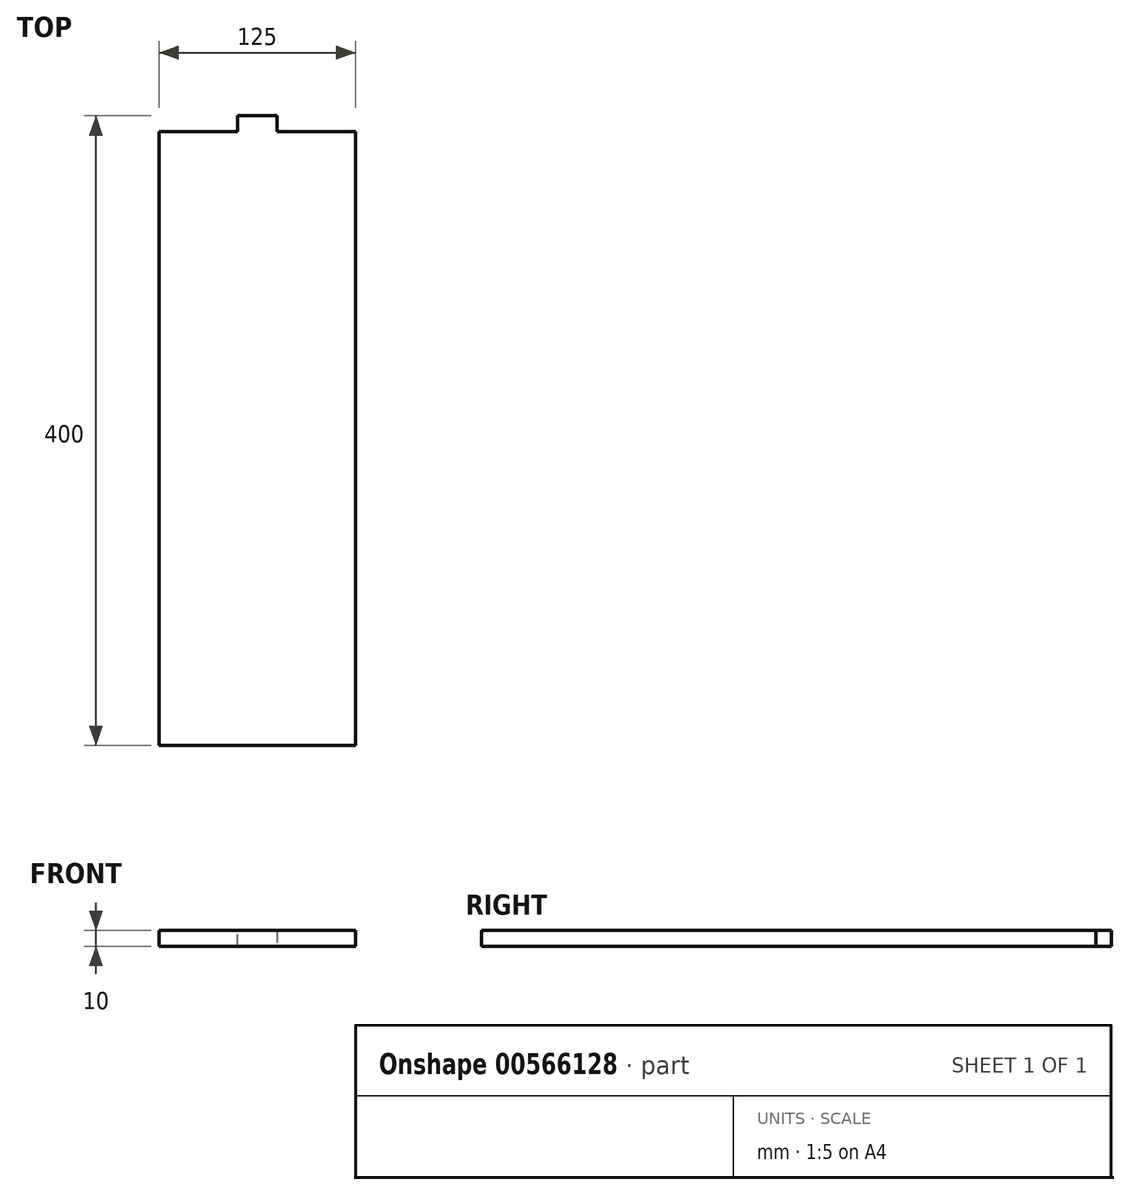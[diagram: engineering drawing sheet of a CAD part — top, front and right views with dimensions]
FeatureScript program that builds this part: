
annotation { "Feature Type Name" : "Feature", "Feature Type Description" : "" }
export const myFeature = defineFeature(function(context is Context, id is Id, definition is map)
    precondition{}
    {
        {
            var Q0;
            Q0=qCreatedBy(makeId("Front.planeOp"),FACE);
            var sketch = newSketch(context, id + "F0", { "sketchPlane" : qUnion([Q0])});
            skLineSegment(sketch, "E0", {"start": v(-250, -65) * mm, "end": v(-125, -65) * mm});
            skLineSegment(sketch, "E1", {"start": v(-125, -65) * mm, "end": v(-125, -75) * mm});
            skLineSegment(sketch, "E2", {"start": v(-125, -75) * mm, "end": v(-250, -75) * mm});
            skLineSegment(sketch, "E3", {"start": v(-250, -75) * mm, "end": v(-250, -65) * mm});
            skSolve(sketch);
        }
        {
            var Q0;
            Q0 = qSketchRegion(id + "F0", true);
            extrude(context, id + "F1", {"entities" : qUnion([Q0]), "depth" : 390 * mm, "offsetDistance" : 25 * mm});
        }
        {
            var Q0;
            Q0=makeQuery(id+"F1.opExtrude","CAP_FACE",FACE,{"disambiguationData":[OSD([sQuery(id+"F0.wireOp",EDGE,"E0"),sQuery(id+"F0.wireOp",EDGE,"E1"),sQuery(id+"F0.wireOp",EDGE,"E2"),sQuery(id+"F0.wireOp",EDGE,"E3")])],"isStart":true});
            var sketch = newSketch(context, id + "F2", { "sketchPlane" : qUnion([Q0])});
            skLineSegment(sketch, "E4", {"start": v(175, -75) * mm, "end": v(200, -75) * mm});
            skLineSegment(sketch, "E5", {"start": v(200, -75) * mm, "end": v(200, -65) * mm});
            skLineSegment(sketch, "E6", {"start": v(200, -65) * mm, "end": v(175, -65) * mm});
            skLineSegment(sketch, "E7", {"start": v(175, -65) * mm, "end": v(175, -75) * mm});
            skSolve(sketch);
        }
        {
            var Q0;
            Q0=makeQuery(id+"F2.imprint","IMPRINT",FACE,{"disambiguationData":[TD([[makeQuery(id+"F2.imprint","IMPRINT",EDGE,{"derivedFrom":sQuery(id+"F2.wireOp",EDGE,"E4")}),1.0]])]});
            extrude(context, id + "F3", {"entities" : qUnion([Q0]), "operationType" : NewBodyOperationType.ADD, "depth" : 10 * mm, "offsetDistance" : 25 * mm});
        }
    });
